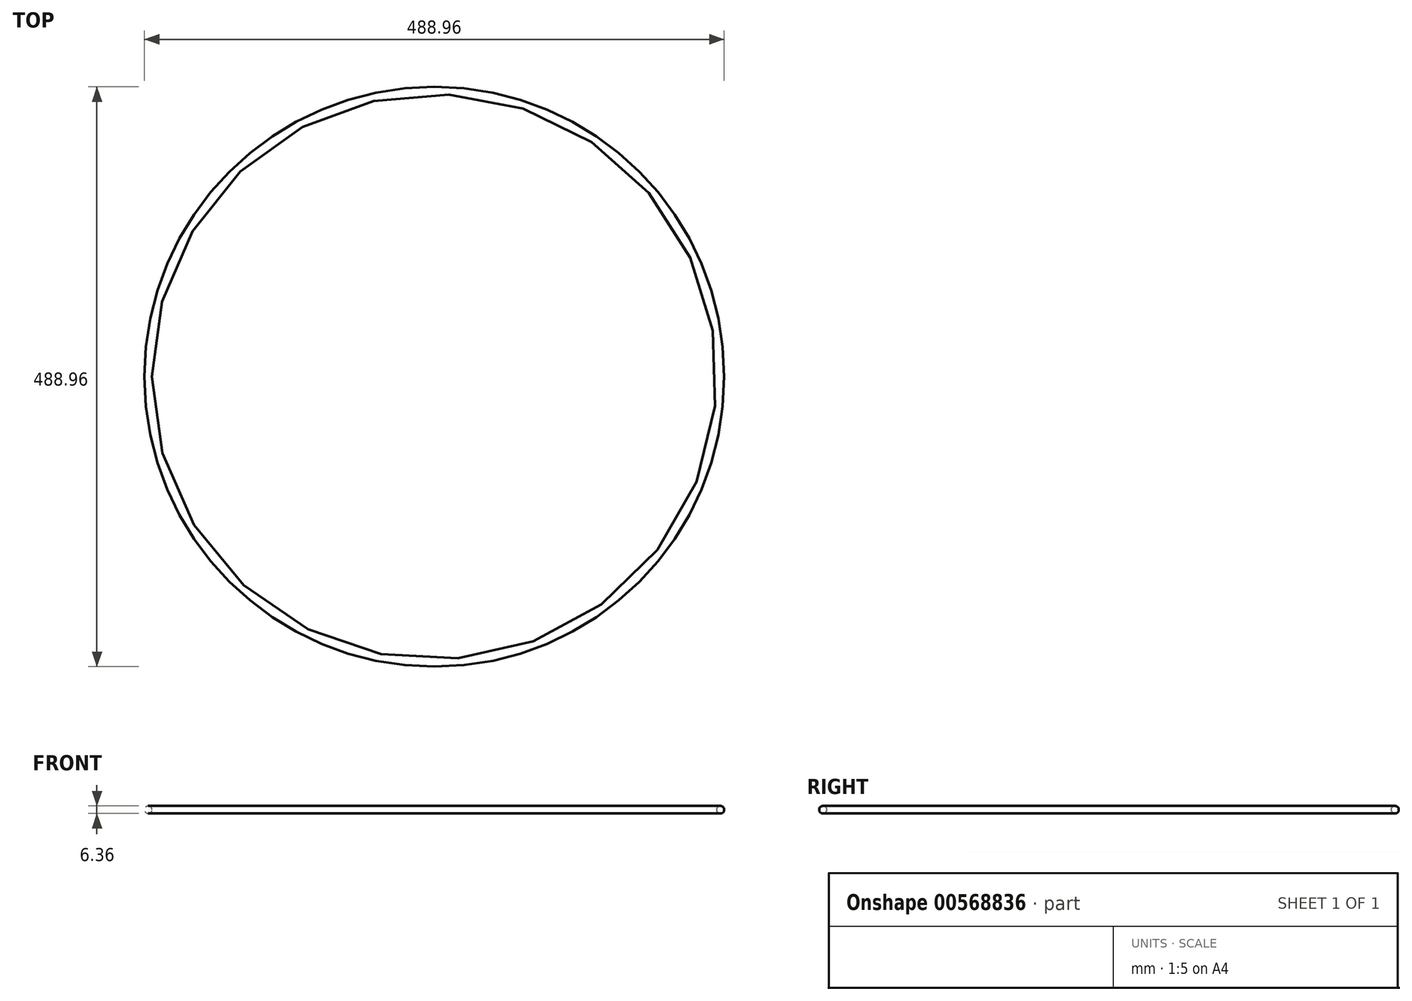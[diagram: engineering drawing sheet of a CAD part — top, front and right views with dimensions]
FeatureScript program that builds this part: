
annotation { "Feature Type Name" : "Feature", "Feature Type Description" : "" }
export const myFeature = defineFeature(function(context is Context, id is Id, definition is map)
    precondition{}
    {
        {
            var Q0;
            Q0=qCreatedBy(makeId("Front.planeOp"),FACE);
            var sketch = newSketch(context, id + "F0", { "sketchPlane" : qUnion([Q0])});
            skCircle(sketch, "E0", {"center": v(241.3, 0) * mm, "radius": 3.18 * mm});
            skLineSegment(sketch, "E1", {"start": v(0, 0) * mm, "end": v(0, 32.12) * mm, "construction": true});
            skSolve(sketch);
        }
        {
            var Q0;
            Q0=makeQuery(id+"F0.imprint","IMPRINT",FACE,{"disambiguationData":[TD([[makeQuery(id+"F0.imprint","IMPRINT",EDGE,{"derivedFrom":sQuery(id+"F0.wireOp",EDGE,"E0")}),1.0]])]});
            var Q1;
            Q1=sQuery(id+"F0.wireOp",EDGE,"E1");
            revolve(context, id + "F1", {"entities" : qUnion([Q0]), "axis" : qUnion([Q1]), "revolveType" : RevolveType.FULL});
        }
    });
